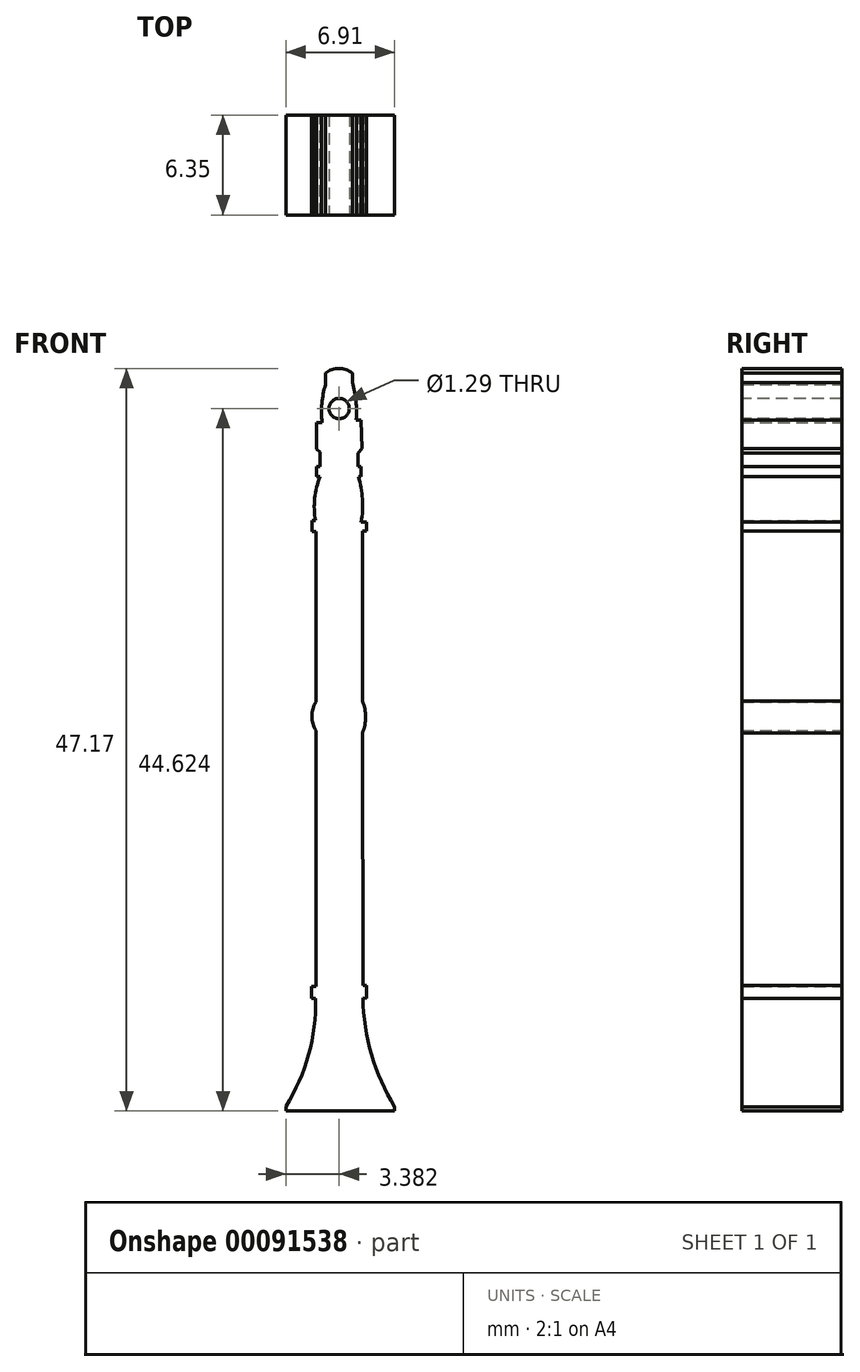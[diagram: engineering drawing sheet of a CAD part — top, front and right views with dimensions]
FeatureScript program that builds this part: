
annotation { "Feature Type Name" : "Feature", "Feature Type Description" : "" }
export const myFeature = defineFeature(function(context is Context, id is Id, definition is map)
    precondition{}
    {
        {
            var Q0;
            Q0=qCreatedBy(makeId("Front.planeOp"),FACE);
            var sketch = newSketch(context, id + "F0", { "sketchPlane" : qUnion([Q0])});
            skLineSegment(sketch, "E0", {"start": v(25.17, 2.72) * mm, "end": v(32.08, 2.72) * mm});
            skLineSegment(sketch, "E1", {"start": v(32.08, 2.72) * mm, "end": v(32.08, 3) * mm});
            skLineSegment(sketch, "E2", {"start": v(25.17, 2.72) * mm, "end": v(25.17, 3.02) * mm});
            skArc(sketch, "E3", {"start": v(25.17, 3.02) * mm, "mid": v(26.61, 6.3) * mm, "end": v(27.06, 9.86) * mm});
            skArc(sketch, "E4", {"start": v(30.06, 9.9) * mm, "mid": v(30.6, 6.3) * mm, "end": v(32.08, 3) * mm});
            skLineSegment(sketch, "E5", {"start": v(27.06, 9.86) * mm, "end": v(26.8, 9.86) * mm});
            skLineSegment(sketch, "E6", {"start": v(26.8, 9.86) * mm, "end": v(26.8, 10.63) * mm});
            skLineSegment(sketch, "E7", {"start": v(26.8, 10.63) * mm, "end": v(27.08, 10.63) * mm});
            skLineSegment(sketch, "E8", {"start": v(27.08, 10.63) * mm, "end": v(27.08, 17.02) * mm});
            skLineSegment(sketch, "E9", {"start": v(27.08, 17.02) * mm, "end": v(27.08, 26.89) * mm});
            skArc(sketch, "E10", {"start": v(27.08, 28.71) * mm, "mid": v(26.82, 27.8) * mm, "end": v(27.08, 26.89) * mm});
            skLineSegment(sketch, "E11", {"start": v(27.08, 28.71) * mm, "end": v(27.08, 39.53) * mm});
            skLineSegment(sketch, "E12", {"start": v(27.08, 39.53) * mm, "end": v(26.82, 39.53) * mm});
            skLineSegment(sketch, "E13", {"start": v(26.82, 39.53) * mm, "end": v(26.82, 40.22) * mm});
            skLineSegment(sketch, "E14", {"start": v(26.82, 40.22) * mm, "end": v(27.04, 40.22) * mm});
            skArc(sketch, "E15", {"start": v(27.34, 43.02) * mm, "mid": v(27, 41.64) * mm, "end": v(27.04, 40.22) * mm});
            skLineSegment(sketch, "E16", {"start": v(27.34, 43.02) * mm, "end": v(27.11, 43.02) * mm});
            skLineSegment(sketch, "E17", {"start": v(27.11, 43.02) * mm, "end": v(27.11, 43.65) * mm});
            skLineSegment(sketch, "E18", {"start": v(27.11, 43.65) * mm, "end": v(27.34, 43.65) * mm});
            skLineSegment(sketch, "E19", {"start": v(27.34, 43.65) * mm, "end": v(27.34, 44.57) * mm});
            skLineSegment(sketch, "E20", {"start": v(27.34, 44.57) * mm, "end": v(27.1, 44.78) * mm});
            skLineSegment(sketch, "E21", {"start": v(27.1, 44.78) * mm, "end": v(27.1, 46.45) * mm});
            skLineSegment(sketch, "E22", {"start": v(27.1, 46.45) * mm, "end": v(27.47, 46.45) * mm});
            skArc(sketch, "E23", {"start": v(27.69, 48.86) * mm, "mid": v(27.45, 47.67) * mm, "end": v(27.47, 46.45) * mm});
            skLineSegment(sketch, "E24", {"start": v(27.69, 48.86) * mm, "end": v(27.69, 49.58) * mm});
            skArc(sketch, "E25", {"start": v(29.39, 49.58) * mm, "mid": v(28.54, 49.89) * mm, "end": v(27.69, 49.58) * mm});
            skLineSegment(sketch, "E26", {"start": v(29.39, 49.58) * mm, "end": v(29.39, 49) * mm});
            skArc(sketch, "E27", {"start": v(29.63, 46.6) * mm, "mid": v(29.62, 47.81) * mm, "end": v(29.39, 49) * mm});
            skLineSegment(sketch, "E28", {"start": v(29.63, 46.6) * mm, "end": v(29.94, 46.6) * mm});
            skLineSegment(sketch, "E29", {"start": v(29.94, 46.6) * mm, "end": v(30, 44.8) * mm});
            skLineSegment(sketch, "E30", {"start": v(30, 44.8) * mm, "end": v(29.76, 44.52) * mm});
            skLineSegment(sketch, "E31", {"start": v(29.76, 44.52) * mm, "end": v(29.76, 43.66) * mm});
            skLineSegment(sketch, "E32", {"start": v(29.76, 43.66) * mm, "end": v(29.95, 43.66) * mm});
            skLineSegment(sketch, "E33", {"start": v(29.95, 43.66) * mm, "end": v(29.95, 43.03) * mm});
            skLineSegment(sketch, "E34", {"start": v(29.95, 43.03) * mm, "end": v(29.77, 43.03) * mm});
            skArc(sketch, "E35", {"start": v(29.95, 40.13) * mm, "mid": v(30.03, 41.59) * mm, "end": v(29.77, 43.03) * mm});
            skLineSegment(sketch, "E36", {"start": v(29.95, 40.13) * mm, "end": v(30.29, 40.13) * mm});
            skLineSegment(sketch, "E37", {"start": v(30.29, 40.13) * mm, "end": v(30.29, 39.55) * mm});
            skLineSegment(sketch, "E38", {"start": v(30.29, 39.55) * mm, "end": v(30.03, 39.55) * mm});
            skLineSegment(sketch, "E39", {"start": v(30.03, 39.55) * mm, "end": v(30.03, 28.76) * mm});
            skArc(sketch, "E40", {"start": v(30.03, 26.74) * mm, "mid": v(30.23, 27.75) * mm, "end": v(30.03, 28.76) * mm});
            skLineSegment(sketch, "E41", {"start": v(30.03, 26.74) * mm, "end": v(30.06, 10.7) * mm});
            skLineSegment(sketch, "E42", {"start": v(30.06, 10.7) * mm, "end": v(30.28, 10.7) * mm});
            skLineSegment(sketch, "E43", {"start": v(30.28, 10.7) * mm, "end": v(30.28, 9.88) * mm});
            skLineSegment(sketch, "E44", {"start": v(30.28, 9.88) * mm, "end": v(30.06, 9.9) * mm});
            skSolve(sketch);
        }
        {
            var Q0;
            Q0 = qSketchRegion(id + "F0", true);
            extrude(context, id + "F1", {"entities" : qUnion([Q0]), "depth" : 6.35 * mm});
        }
        {
            var Q0;
            Q0=makeQuery(id+"F1.opExtrude","CAP_FACE",FACE,{"disambiguationData":[OSD([sQuery(id+"F0.wireOp",EDGE,"E0"),sQuery(id+"F0.wireOp",EDGE,"E1"),sQuery(id+"F0.wireOp",EDGE,"E2"),sQuery(id+"F0.wireOp",EDGE,"E3"),sQuery(id+"F0.wireOp",EDGE,"E4"),sQuery(id+"F0.wireOp",EDGE,"E5"),sQuery(id+"F0.wireOp",EDGE,"E6"),sQuery(id+"F0.wireOp",EDGE,"E7"),sQuery(id+"F0.wireOp",EDGE,"E8"),sQuery(id+"F0.wireOp",EDGE,"E9"),sQuery(id+"F0.wireOp",EDGE,"E10"),sQuery(id+"F0.wireOp",EDGE,"E11"),sQuery(id+"F0.wireOp",EDGE,"E12"),sQuery(id+"F0.wireOp",EDGE,"E13"),sQuery(id+"F0.wireOp",EDGE,"E14"),sQuery(id+"F0.wireOp",EDGE,"E15"),sQuery(id+"F0.wireOp",EDGE,"E16"),sQuery(id+"F0.wireOp",EDGE,"E17"),sQuery(id+"F0.wireOp",EDGE,"E18"),sQuery(id+"F0.wireOp",EDGE,"E19"),sQuery(id+"F0.wireOp",EDGE,"E20"),sQuery(id+"F0.wireOp",EDGE,"E21"),sQuery(id+"F0.wireOp",EDGE,"E22"),sQuery(id+"F0.wireOp",EDGE,"E23"),sQuery(id+"F0.wireOp",EDGE,"E24"),sQuery(id+"F0.wireOp",EDGE,"E25"),sQuery(id+"F0.wireOp",EDGE,"E26"),sQuery(id+"F0.wireOp",EDGE,"E27"),sQuery(id+"F0.wireOp",EDGE,"E28"),sQuery(id+"F0.wireOp",EDGE,"E29"),sQuery(id+"F0.wireOp",EDGE,"E30"),sQuery(id+"F0.wireOp",EDGE,"E31"),sQuery(id+"F0.wireOp",EDGE,"E32"),sQuery(id+"F0.wireOp",EDGE,"E33"),sQuery(id+"F0.wireOp",EDGE,"E34"),sQuery(id+"F0.wireOp",EDGE,"E35"),sQuery(id+"F0.wireOp",EDGE,"E36"),sQuery(id+"F0.wireOp",EDGE,"E37"),sQuery(id+"F0.wireOp",EDGE,"E38"),sQuery(id+"F0.wireOp",EDGE,"E39"),sQuery(id+"F0.wireOp",EDGE,"E40"),sQuery(id+"F0.wireOp",EDGE,"E41"),sQuery(id+"F0.wireOp",EDGE,"E42"),sQuery(id+"F0.wireOp",EDGE,"E43"),sQuery(id+"F0.wireOp",EDGE,"E44")])],"isStart":false});
            var sketch = newSketch(context, id + "F2", { "sketchPlane" : qUnion([Q0])});
            skLineSegment(sketch, "E45", {"start": v(27.47, 46.45) * mm, "end": v(29.63, 46.6) * mm, "construction": true});
            skLineSegment(sketch, "E46", {"start": v(28.55, 46.53) * mm, "end": v(28.55, 47.34) * mm, "construction": true});
            skCircle(sketch, "E47", {"center": v(28.55, 47.34) * mm, "radius": 0.64 * mm});
            skSolve(sketch);
        }
        {
            var Q0;
            Q0=makeQuery(id+"F2.imprint","IMPRINT",FACE,{"disambiguationData":[TD([[makeQuery(id+"F2.imprint","IMPRINT",EDGE,{"derivedFrom":sQuery(id+"F2.wireOp",EDGE,"E47")}),1.0]])]});
            extrude(context, id + "F3", {"entities" : qUnion([Q0]), "operationType" : NewBodyOperationType.REMOVE, "oppositeDirection" : true, "depth" : 25.4 * mm});
        }
    });
